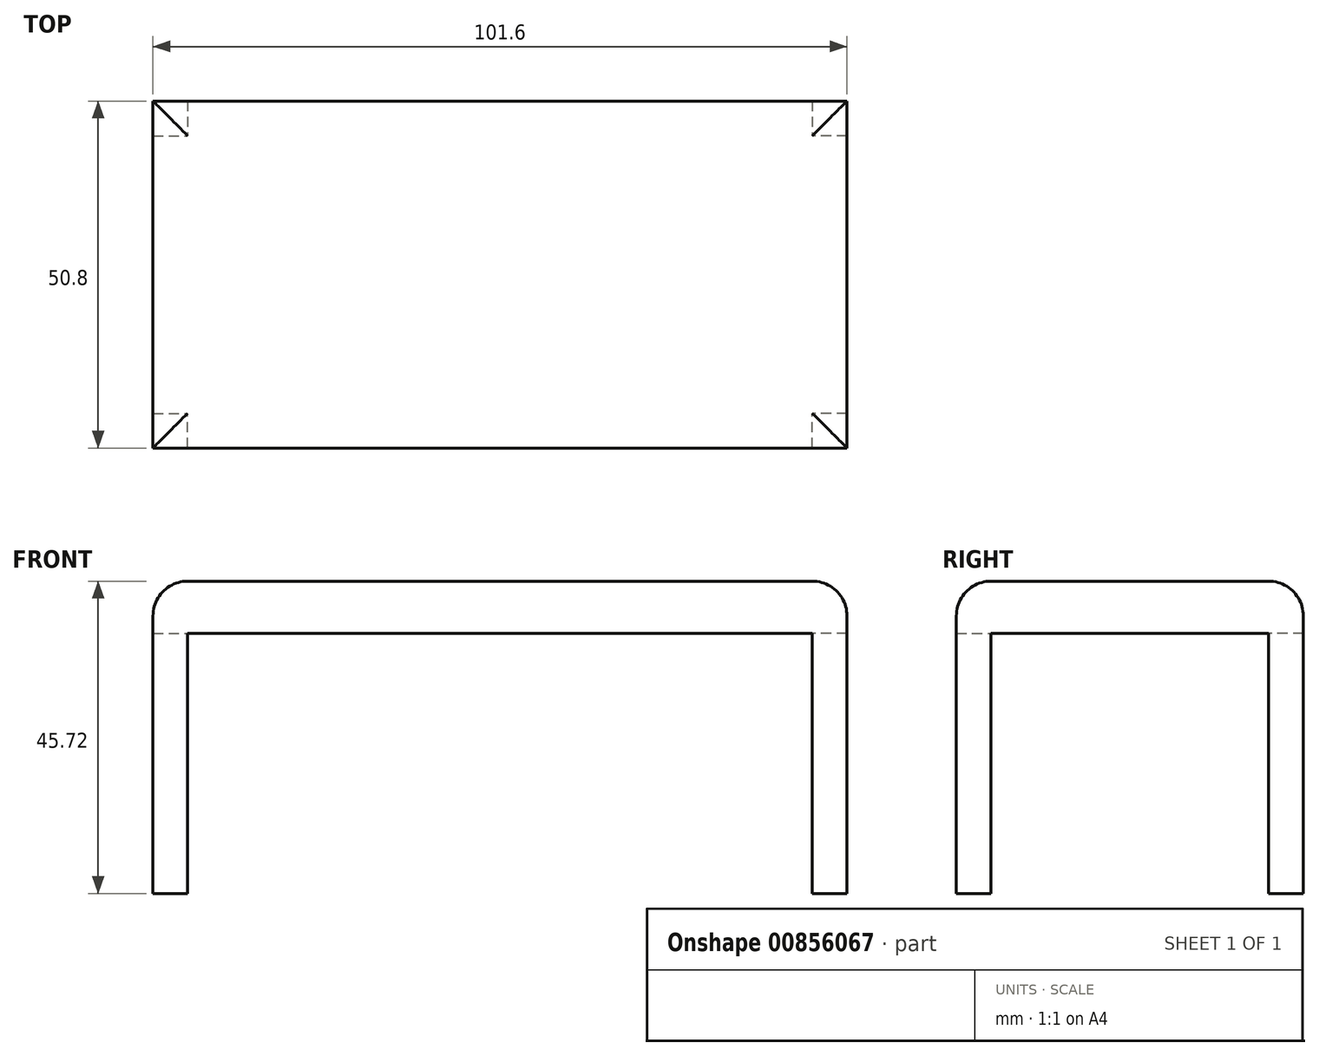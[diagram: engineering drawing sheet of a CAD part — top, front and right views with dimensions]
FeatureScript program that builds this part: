
annotation { "Feature Type Name" : "Feature", "Feature Type Description" : "" }
export const myFeature = defineFeature(function(context is Context, id is Id, definition is map)
    precondition{}
    {
        {
            var Q0;
            Q0=qCreatedBy(makeId("Top.planeOp"),FACE);
            var sketch = newSketch(context, id + "F0", { "sketchPlane" : qUnion([Q0])});
            skLineSegment(sketch, "E0.bottom", {"start": v(-59.99, 13.36) * mm, "end": v(41.61, 13.36) * mm});
            skLineSegment(sketch, "E0.top", {"start": v(-59.99, -37.44) * mm, "end": v(41.61, -37.44) * mm});
            skLineSegment(sketch, "E0.left", {"start": v(-59.99, 13.36) * mm, "end": v(-59.99, -37.44) * mm});
            skLineSegment(sketch, "E0.right", {"start": v(41.61, 13.36) * mm, "end": v(41.61, -37.44) * mm});
            skSolve(sketch);
        }
        {
            var Q0;
            Q0=makeQuery(id+"F0.imprint","IMPRINT",FACE,{"disambiguationData":[TD([[makeQuery(id+"F0.imprint","IMPRINT",EDGE,{"derivedFrom":sQuery(id+"F0.wireOp",EDGE,"E0.bottom")}),-1.0]])]});
            extrude(context, id + "F1", {"entities" : qUnion([Q0]), "depth" : 7.62 * mm, "offsetDistance" : 25.4 * mm});
        }
        {
            var Q0;
            Q0=makeQuery(id+"F1.opExtrude","CAP_EDGE",EDGE,{"disambiguationData":[OSD([sQuery(id+"F0.wireOp",EDGE,"E0.top")])],"isStart":false});
            var Q1;
            Q1=makeQuery(id+"F1.opExtrude","CAP_EDGE",EDGE,{"disambiguationData":[OSD([sQuery(id+"F0.wireOp",EDGE,"E0.left")])],"isStart":false});
            var Q2;
            Q2=makeQuery(id+"F1.opExtrude","CAP_EDGE",EDGE,{"disambiguationData":[OSD([sQuery(id+"F0.wireOp",EDGE,"E0.bottom")])],"isStart":false});
            var Q3;
            Q3=makeQuery(id+"F1.opExtrude","CAP_EDGE",EDGE,{"disambiguationData":[OSD([sQuery(id+"F0.wireOp",EDGE,"E0.right")])],"isStart":false});
            fillet(context, id + "F2", {"entities" : qUnion([Q0, Q1, Q2, Q3]), "radius" : 5.08 * mm, "tangentPropagation" : true, "allowEdgeOverflow" : false});
        }
        {
            var Q0;
            Q0=makeQuery(id+"F1.opExtrude","CAP_FACE",FACE,{"disambiguationData":[OSD([sQuery(id+"F0.wireOp",EDGE,"E0.bottom"),sQuery(id+"F0.wireOp",EDGE,"E0.top"),sQuery(id+"F0.wireOp",EDGE,"E0.left"),sQuery(id+"F0.wireOp",EDGE,"E0.right")])],"isStart":true});
            var sketch = newSketch(context, id + "F3", { "sketchPlane" : qUnion([Q0])});
            skLineSegment(sketch, "E1.bottom", {"start": v(-59.99, 37.44) * mm, "end": v(-54.9, 37.44) * mm});
            skLineSegment(sketch, "E1.top", {"start": v(-59.99, 32.36) * mm, "end": v(-54.9, 32.36) * mm});
            skLineSegment(sketch, "E1.left", {"start": v(-59.99, 37.44) * mm, "end": v(-59.99, 32.36) * mm});
            skLineSegment(sketch, "E1.right", {"start": v(-54.9, 37.44) * mm, "end": v(-54.9, 32.36) * mm});
            skLineSegment(sketch, "E2.bottom", {"start": v(-59.99, -13.36) * mm, "end": v(-54.9, -13.36) * mm});
            skLineSegment(sketch, "E2.top", {"start": v(-59.99, -8.28) * mm, "end": v(-54.9, -8.28) * mm});
            skLineSegment(sketch, "E2.left", {"start": v(-59.99, -13.36) * mm, "end": v(-59.99, -8.28) * mm});
            skLineSegment(sketch, "E2.right", {"start": v(-54.9, -13.36) * mm, "end": v(-54.9, -8.28) * mm});
            skLineSegment(sketch, "E3.bottom", {"start": v(41.61, -13.36) * mm, "end": v(36.53, -13.36) * mm});
            skLineSegment(sketch, "E3.top", {"start": v(41.61, 0) * mm, "end": v(36.53, 0) * mm});
            skLineSegment(sketch, "E3.left", {"start": v(41.61, -13.36) * mm, "end": v(41.61, 0) * mm});
            skLineSegment(sketch, "E3.right", {"start": v(36.53, -13.36) * mm, "end": v(36.53, 0) * mm});
            skLineSegment(sketch, "E4.bottom", {"start": v(41.61, 37.44) * mm, "end": v(36.53, 37.44) * mm});
            skLineSegment(sketch, "E4.top", {"start": v(41.61, 32.36) * mm, "end": v(36.53, 32.36) * mm});
            skLineSegment(sketch, "E4.left", {"start": v(41.61, 37.44) * mm, "end": v(41.61, 32.36) * mm});
            skLineSegment(sketch, "E4.right", {"start": v(36.53, 37.44) * mm, "end": v(36.53, 32.36) * mm});
            skLineSegment(sketch, "E5.top", {"start": v(41.61, -8.28) * mm, "end": v(36.53, -8.28) * mm});
            skLineSegment(sketch, "E5.left", {"start": v(41.61, -13.36) * mm, "end": v(41.61, -8.28) * mm});
            skLineSegment(sketch, "E5.right", {"start": v(36.53, -13.36) * mm, "end": v(36.53, -8.28) * mm});
            skSolve(sketch);
        }
        {
            var Q0;
            Q0=makeQuery(id+"F3.imprint","IMPRINT",FACE,{"disambiguationData":[TD([[makeQuery(id+"F3.imprint","IMPRINT",EDGE,{"derivedFrom":sQuery(id+"F3.wireOp",EDGE,"E3.bottom")}),1.0]])]});
            var Q1;
            Q1=makeQuery(id+"F3.imprint","IMPRINT",FACE,{"disambiguationData":[TD([[makeQuery(id+"F3.imprint","IMPRINT",EDGE,{"derivedFrom":sQuery(id+"F3.wireOp",EDGE,"E4.bottom")}),-1.0]])]});
            var Q2;
            Q2=makeQuery(id+"F3.imprint","IMPRINT",FACE,{"disambiguationData":[TD([[makeQuery(id+"F3.imprint","IMPRINT",EDGE,{"derivedFrom":sQuery(id+"F3.wireOp",EDGE,"E2.bottom")}),1.0]])]});
            var Q3;
            Q3=makeQuery(id+"F3.imprint","IMPRINT",FACE,{"disambiguationData":[TD([[makeQuery(id+"F3.imprint","IMPRINT",EDGE,{"derivedFrom":sQuery(id+"F3.wireOp",EDGE,"E1.bottom")}),-1.0]])]});
            extrude(context, id + "F4", {"entities" : qUnion([Q0, Q1, Q2, Q3]), "operationType" : NewBodyOperationType.ADD, "depth" : 38.1 * mm, "offsetDistance" : 25.4 * mm});
        }
    });
